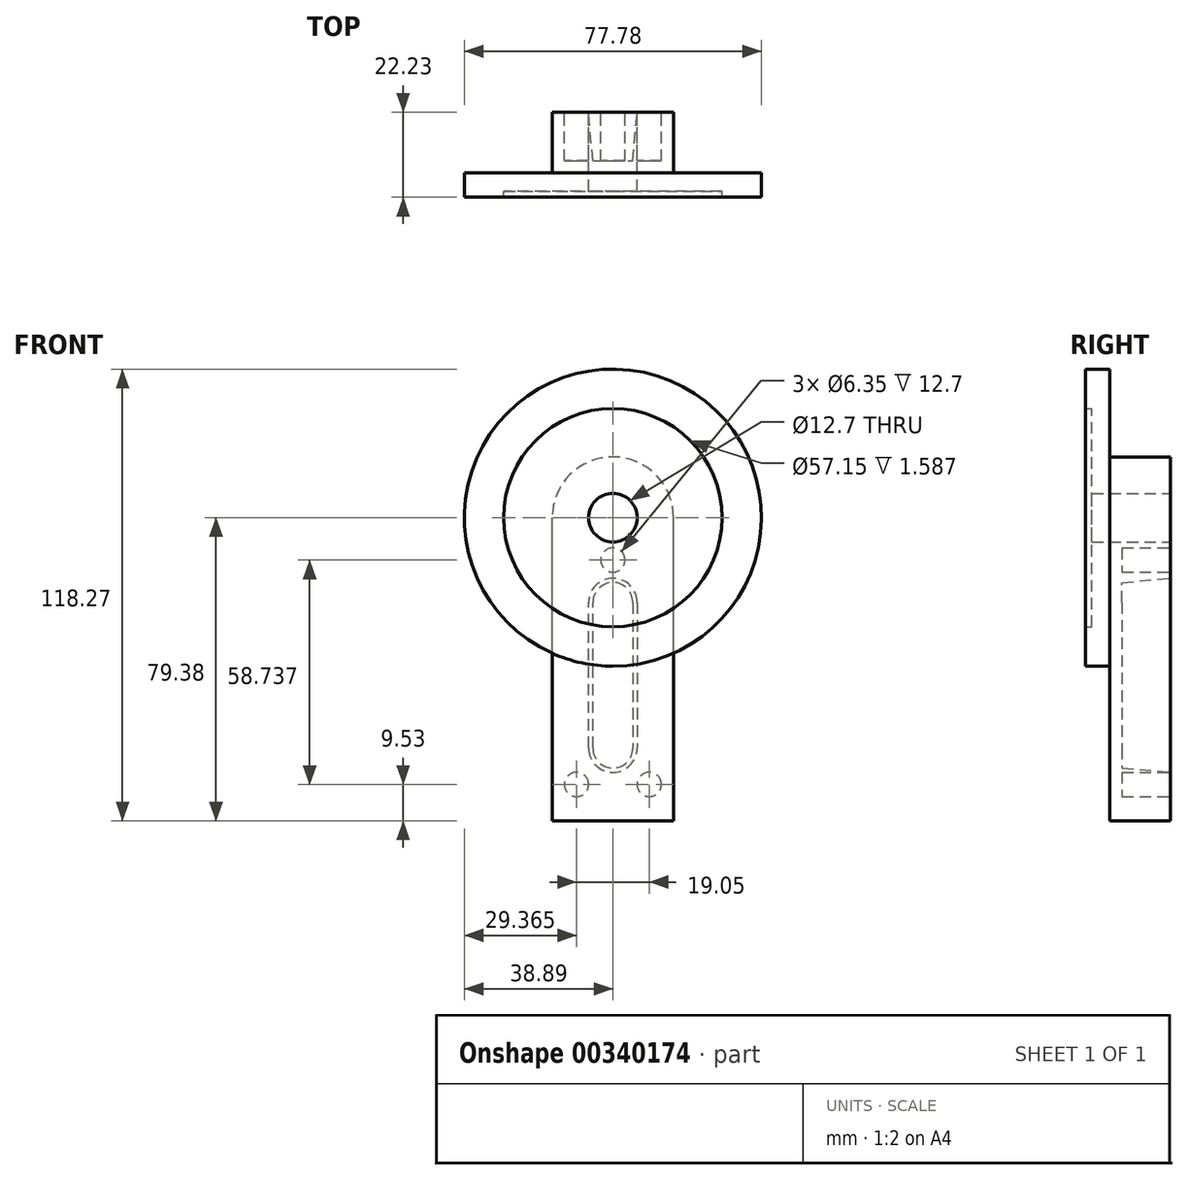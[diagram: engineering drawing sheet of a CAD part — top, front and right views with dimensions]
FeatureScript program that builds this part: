
annotation { "Feature Type Name" : "Feature", "Feature Type Description" : "" }
export const myFeature = defineFeature(function(context is Context, id is Id, definition is map)
    precondition{}
    {
        {
            var Q0;
            Q0=qCreatedBy(makeId("Front.planeOp"),FACE);
            var sketch = newSketch(context, id + "F0", { "sketchPlane" : qUnion([Q0])});
            skCircle(sketch, "E0", {"center": v(0, 0) * mm, "radius": 38.9 * mm});
            skCircle(sketch, "E1", {"center": v(0, 0) * mm, "radius": 6.35 * mm});
            skSolve(sketch);
        }
        {
            var Q0;
            Q0 = qSketchRegion(id + "F0", true);
            extrude(context, id + "F1", {"entities" : qUnion([Q0]), "depth" : 4.76 * mm});
        }
        {
            var Q0;
            Q0=makeQuery(id+"F1.opExtrude","CAP_FACE",FACE,{"disambiguationData":[OSD([sQuery(id+"F0.wireOp",EDGE,"E0"),sQuery(id+"F0.wireOp",EDGE,"E1")])],"isStart":false});
            var sketch = newSketch(context, id + "F2", { "sketchPlane" : qUnion([Q0])});
            skCircle(sketch, "E2", {"center": v(0, 0) * mm, "radius": 28.58 * mm});
            skCircle(sketch, "E3.0.0", {"center": v(0, 0) * mm, "radius": 38.9 * mm});
            skSolve(sketch);
        }
        {
            var Q0;
            Q0 = qSketchRegion(id + "F2", true);
            extrude(context, id + "F3", {"entities" : qUnion([Q0]), "operationType" : NewBodyOperationType.ADD, "depth" : 1.59 * mm});
        }
        {
            var Q0;
            Q0=makeQuery(id+"F1.opExtrude","CAP_FACE",FACE,{"disambiguationData":[OSD([sQuery(id+"F0.wireOp",EDGE,"E0"),sQuery(id+"F0.wireOp",EDGE,"E1")])],"isStart":true});
            var sketch = newSketch(context, id + "F4", { "sketchPlane" : qUnion([Q0])});
            skLineSegment(sketch, "E4.bottom", {"start": v(15.88, -79.38) * mm, "end": v(-15.87, -79.38) * mm});
            skLineSegment(sketch, "E4.top", {"start": v(15.87, 79.37) * mm, "end": v(-15.88, 79.37) * mm});
            skLineSegment(sketch, "E4.left", {"start": v(15.88, -79.38) * mm, "end": v(15.88, 79.37) * mm});
            skLineSegment(sketch, "E4.right", {"start": v(-15.88, -79.38) * mm, "end": v(-15.88, 79.37) * mm});
            skPoint(sketch, "E4.middle", {"position": v(0, 0) * mm});
            skCircle(sketch, "E5", {"center": v(0, 0) * mm, "radius": 15.88 * mm});
            skSolve(sketch);
        }
        {
            var Q0;
            {var subQ0=sQuery(id+"F4.wireOp",EDGE,"E4.bottom");Q0=makeQuery(id+"F4.imprint","IMPRINT",FACE,{"disambiguationData":[TD([[makeQuery(id+"F4.imprint","IMPRINT",EDGE,{"derivedFrom":subQ0}),-1.0]])]});}
            var Q1;
            {var subQ0=sQuery(id+"F4.wireOp",EDGE,"E5");var subQ1=sQuery(id+"F4.wireOp",EDGE,"E4.left");var subQ2=makeQuery(id+"F4.imprint","INTERSECT",VERTEX,{"derivedFrom":[subQ1,subQ0]});Q1=makeQuery(id+"F4.imprint","IMPRINT",FACE,{"disambiguationData":[TD([[makeQuery(id+"F4.imprint","IMPRINT",EDGE,{"disambiguationData":[TD([[subQ2,1.0]])],"derivedFrom":subQ1}),1.0]])]});}
            var Q2;
            Q2=makeQuery(id+"F4.imprint","IMPRINT",FACE,{"disambiguationData":[TD([[makeQuery(id+"F4.imprint","IMPRINT",EDGE,{"derivedFrom":makeQuery(id+"F1.opExtrude","CAP_EDGE",EDGE,{"disambiguationData":[OSD([sQuery(id+"F0.wireOp",EDGE,"E1")])],"isStart":true})}),1.0]])]});
            extrude(context, id + "F5", {"entities" : qUnion([Q0, Q1, Q2]), "operationType" : NewBodyOperationType.ADD, "depth" : 15.88 * mm});
        }
        {
            var Q0;
            Q0=makeQuery(id+"F5.opExtrude","CAP_FACE",FACE,{"disambiguationData":[OSD([sQuery(id+"F0.wireOp",EDGE,"E1"),sQuery(id+"F4.wireOp",EDGE,"E4.bottom"),sQuery(id+"F4.wireOp",EDGE,"E4.left"),sQuery(id+"F4.wireOp",EDGE,"E4.right"),sQuery(id+"F4.wireOp",EDGE,"E5")])],"isStart":false});
            var sketch = newSketch(context, id + "F6", { "sketchPlane" : qUnion([Q0])});
            skLineSegment(sketch, "E6", {"start": v(0, -79.38) * mm, "end": v(0, 0) * mm});
            skLineSegment(sketch, "E7.bottom", {"start": v(6.35, -60.33) * mm, "end": v(-6.35, -60.33) * mm});
            skLineSegment(sketch, "E7.top", {"start": v(6.35, -22.23) * mm, "end": v(-6.35, -22.23) * mm});
            skLineSegment(sketch, "E7.left", {"start": v(6.35, -60.33) * mm, "end": v(6.35, -22.23) * mm});
            skLineSegment(sketch, "E7.right", {"start": v(-6.35, -60.33) * mm, "end": v(-6.35, -22.23) * mm});
            skPoint(sketch, "E7.middle", {"position": v(0, -41.28) * mm});
            skCircle(sketch, "E8", {"center": v(0, -22.23) * mm, "radius": 6.35 * mm});
            skCircle(sketch, "E9", {"center": v(0, -60.33) * mm, "radius": 6.35 * mm});
            skSolve(sketch);
        }
        {
            var Q0;
            Q0 = qSketchRegion(id + "F6", true);
            extrude(context, id + "F7", {"entities" : qUnion([Q0]), "operationType" : NewBodyOperationType.REMOVE, "oppositeDirection" : true, "depth" : 12.7 * mm, "hasDraft" : true, "draftAngle" : 5 * degree, "draftPullDirection" : true});
        }
        {
            var Q0;
            Q0=makeQuery(id+"F5.opExtrude","CAP_FACE",FACE,{"disambiguationData":[OSD([sQuery(id+"F0.wireOp",EDGE,"E1"),sQuery(id+"F4.wireOp",EDGE,"E4.bottom"),sQuery(id+"F4.wireOp",EDGE,"E4.left"),sQuery(id+"F4.wireOp",EDGE,"E4.right"),sQuery(id+"F4.wireOp",EDGE,"E5")])],"isStart":false});
            var sketch = newSketch(context, id + "F8", { "sketchPlane" : qUnion([Q0])});
            skLineSegment(sketch, "E10", {"start": v(0, 0) * mm, "end": v(0, -69.85) * mm});
            skLineSegment(sketch, "E11", {"start": v(9.53, -69.85) * mm, "end": v(-9.52, -69.85) * mm});
            skCircle(sketch, "E12", {"center": v(0, -11.11) * mm, "radius": 3.18 * mm});
            skCircle(sketch, "E13", {"center": v(-9.52, -69.85) * mm, "radius": 3.18 * mm});
            skCircle(sketch, "E14", {"center": v(9.53, -69.85) * mm, "radius": 3.18 * mm});
            skSolve(sketch);
        }
        {
            var Q0;
            Q0 = qSketchRegion(id + "F8", true);
            extrude(context, id + "F9", {"entities" : qUnion([Q0]), "operationType" : NewBodyOperationType.REMOVE, "oppositeDirection" : true, "depth" : 12.7 * mm});
        }
    });
